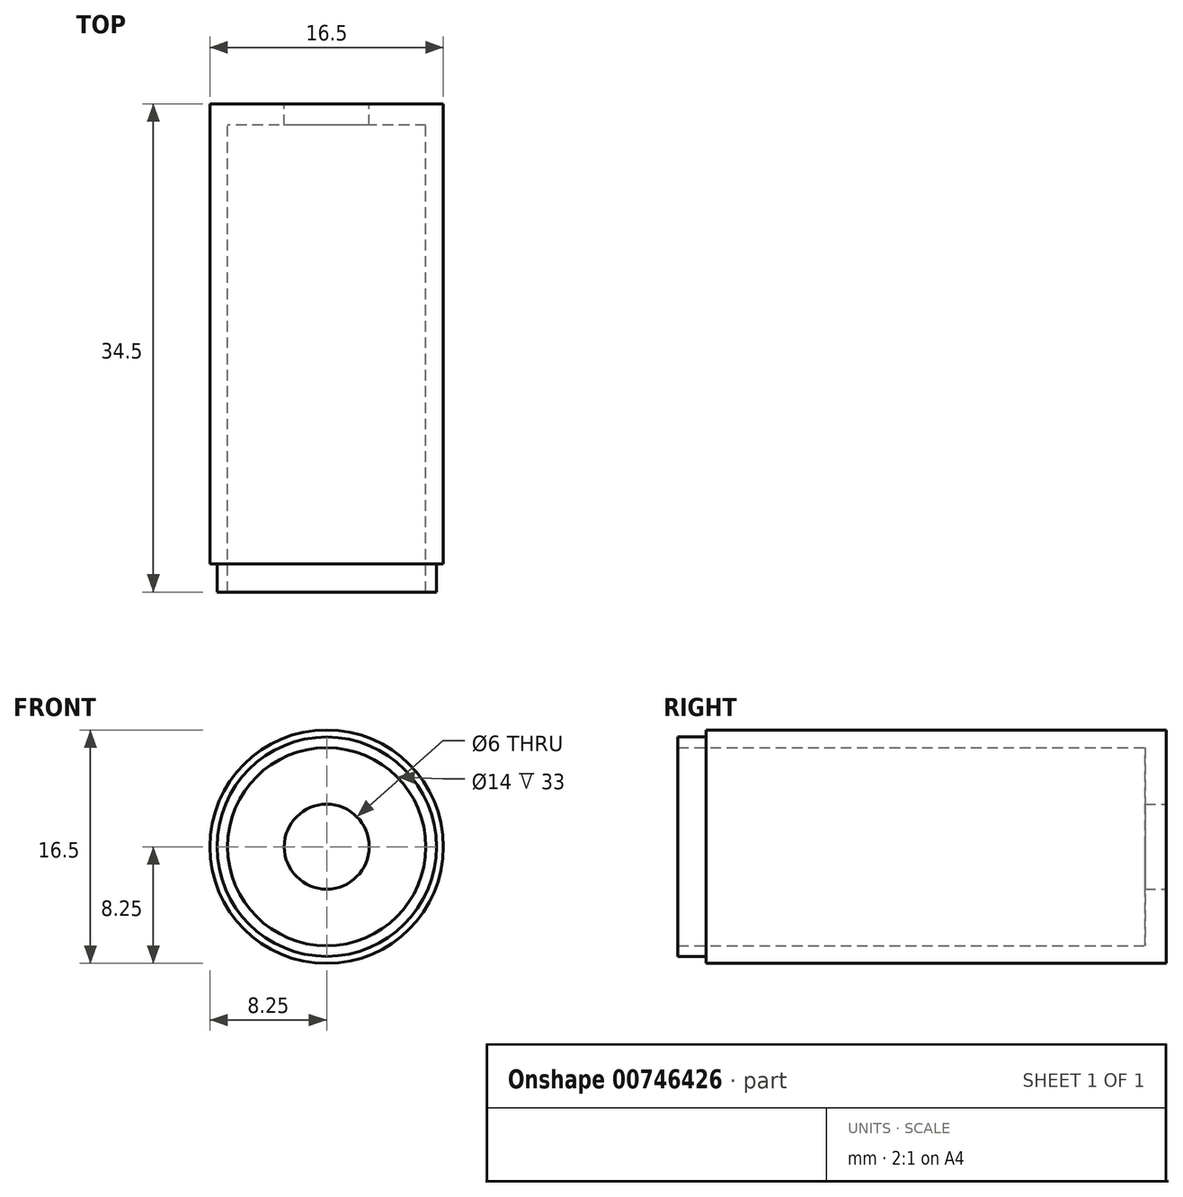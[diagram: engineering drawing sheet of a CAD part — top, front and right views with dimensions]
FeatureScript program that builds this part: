
annotation { "Feature Type Name" : "Feature", "Feature Type Description" : "" }
export const myFeature = defineFeature(function(context is Context, id is Id, definition is map)
    precondition{}
    {
        {
            var Q0;
            Q0=qCreatedBy(makeId("Top.planeOp"),FACE);
            var sketch = newSketch(context, id + "F0", { "sketchPlane" : qUnion([Q0])});
            skCircle(sketch, "E0", {"center": v(0, 0) * mm, "radius": 8.25 * mm});
            skCircle(sketch, "E1", {"center": v(0, 0) * mm, "radius": 3 * mm});
            skSolve(sketch);
        }
        {
            var Q0;
            Q0 = qSketchRegion(id + "F0", true);
            extrude(context, id + "F1", {"entities" : qUnion([Q0]), "depth" : 1.5 * mm, "offsetDistance" : 25.4 * mm});
        }
        {
            var Q0;
            Q0=makeQuery(id+"F1.opExtrude","CAP_FACE",FACE,{"disambiguationData":[OSD([sQuery(id+"F0.wireOp",EDGE,"E0"),sQuery(id+"F0.wireOp",EDGE,"E1")])],"isStart":false});
            var sketch = newSketch(context, id + "F2", { "sketchPlane" : qUnion([Q0])});
            skCircle(sketch, "E2", {"center": v(0, 0) * mm, "radius": 8.25 * mm});
            skCircle(sketch, "E3", {"center": v(0, 0) * mm, "radius": 7 * mm});
            skSolve(sketch);
        }
        {
            var Q0;
            Q0 = qSketchRegion(id + "F2", true);
            extrude(context, id + "F3", {"entities" : qUnion([Q0]), "operationType" : NewBodyOperationType.ADD, "depth" : 31 * mm, "offsetDistance" : 25.4 * mm});
        }
        {
            var Q0;
            Q0=makeQuery(id+"F3.opExtrude","CAP_FACE",FACE,{"disambiguationData":[OSD([sQuery(id+"F2.wireOp",EDGE,"E2"),sQuery(id+"F2.wireOp",EDGE,"E3")])],"isStart":false});
            var sketch = newSketch(context, id + "F4", { "sketchPlane" : qUnion([Q0])});
            skCircle(sketch, "E4", {"center": v(0, 0) * mm, "radius": 7 * mm});
            skCircle(sketch, "E5", {"center": v(0, 0) * mm, "radius": 7.75 * mm});
            skSolve(sketch);
        }
        {
            var Q0;
            Q0 = qSketchRegion(id + "F4", true);
            extrude(context, id + "F5", {"entities" : qUnion([Q0]), "operationType" : NewBodyOperationType.ADD, "depth" : 2 * mm, "offsetDistance" : 25.4 * mm});
        }
        {
            var Q0;
            Q0=qCreatedBy(makeId("Top.planeOp"),FACE);
            var sketch = newSketch(context, id + "F6", { "sketchPlane" : qUnion([Q0])});
            skLineSegment(sketch, "E6", {"start": v(-25.14, 0) * mm, "end": v(37.79, 0) * mm});
            skSolve(sketch);
        }
        {
            var Q0;
            Q0=makeQuery(id+"F1.opExtrude","SWEPT_BODY",BODY,{"disambiguationData":[OSD([sQuery(id+"F0.wireOp",EDGE,"E0"),sQuery(id+"F0.wireOp",EDGE,"E1")])]});
            var Q1;
            Q1=sQuery(id+"F6.wireOp",EDGE,"E6");
            transform(context, id + "F7", {"entities" : qUnion([Q0]), "transformType" : TransformType.ROTATION, "transformAxis" : qUnion([Q1]), "angle" : 90 * degree, "makeCopy" : false});
        }
    });
